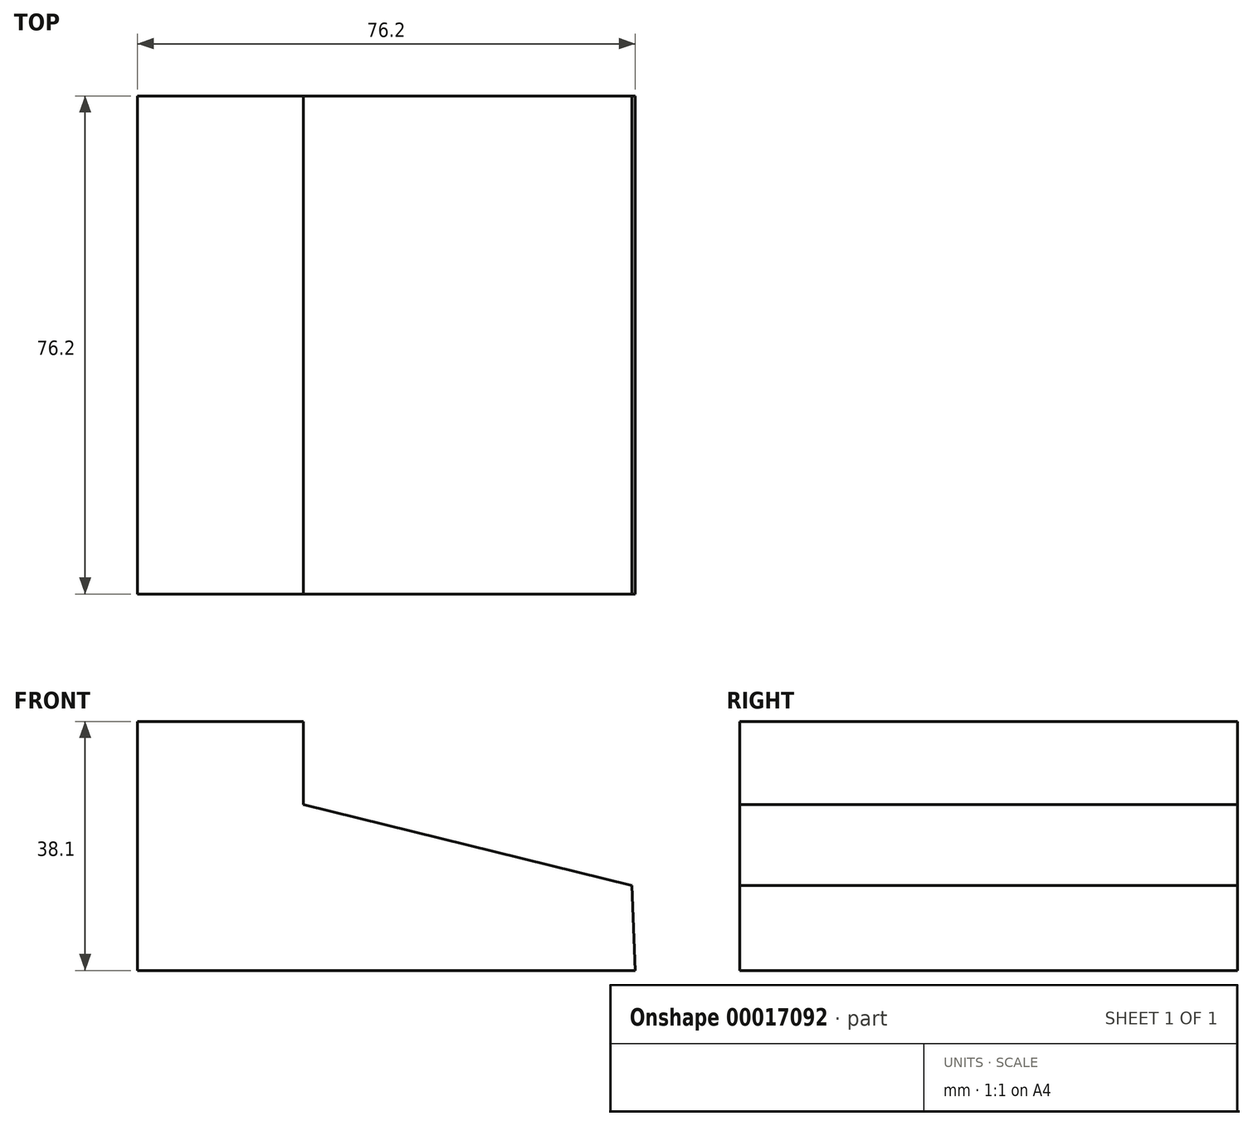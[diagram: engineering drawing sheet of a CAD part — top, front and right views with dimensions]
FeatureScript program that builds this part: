
annotation { "Feature Type Name" : "Feature", "Feature Type Description" : "" }
export const myFeature = defineFeature(function(context is Context, id is Id, definition is map)
    precondition{}
    {
        {
            var Q0;
            Q0=qCreatedBy(makeId("Front.planeOp"),FACE);
            var sketch = newSketch(context, id + "F0", { "sketchPlane" : qUnion([Q0])});
            skLineSegment(sketch, "E0", {"start": v(-53.51, 25) * mm, "end": v(-53.51, -13.1) * mm});
            skLineSegment(sketch, "E1", {"start": v(-53.51, -13.1) * mm, "end": v(22.69, -13.1) * mm});
            skLineSegment(sketch, "E2", {"start": v(-53.51, 25) * mm, "end": v(-28.11, 25) * mm});
            skLineSegment(sketch, "E3", {"start": v(-28.11, 25) * mm, "end": v(-28.11, 12.3) * mm});
            skLineSegment(sketch, "E4", {"start": v(-28.11, 12.3) * mm, "end": v(22.2, -0.1) * mm});
            skLineSegment(sketch, "E5", {"start": v(22.69, -13.1) * mm, "end": v(22.2, -0.1) * mm});
            skSolve(sketch);
        }
        {
            var Q0;
            Q0=makeQuery(id+"F0.imprint","IMPRINT",FACE,{"disambiguationData":[TD([[makeQuery(id+"F0.imprint","IMPRINT",EDGE,{"derivedFrom":sQuery(id+"F0.wireOp",EDGE,"E0")}),1.0]])]});
            extrude(context, id + "F1", {"entities" : qUnion([Q0]), "depth" : 76.2 * mm});
        }
    });
